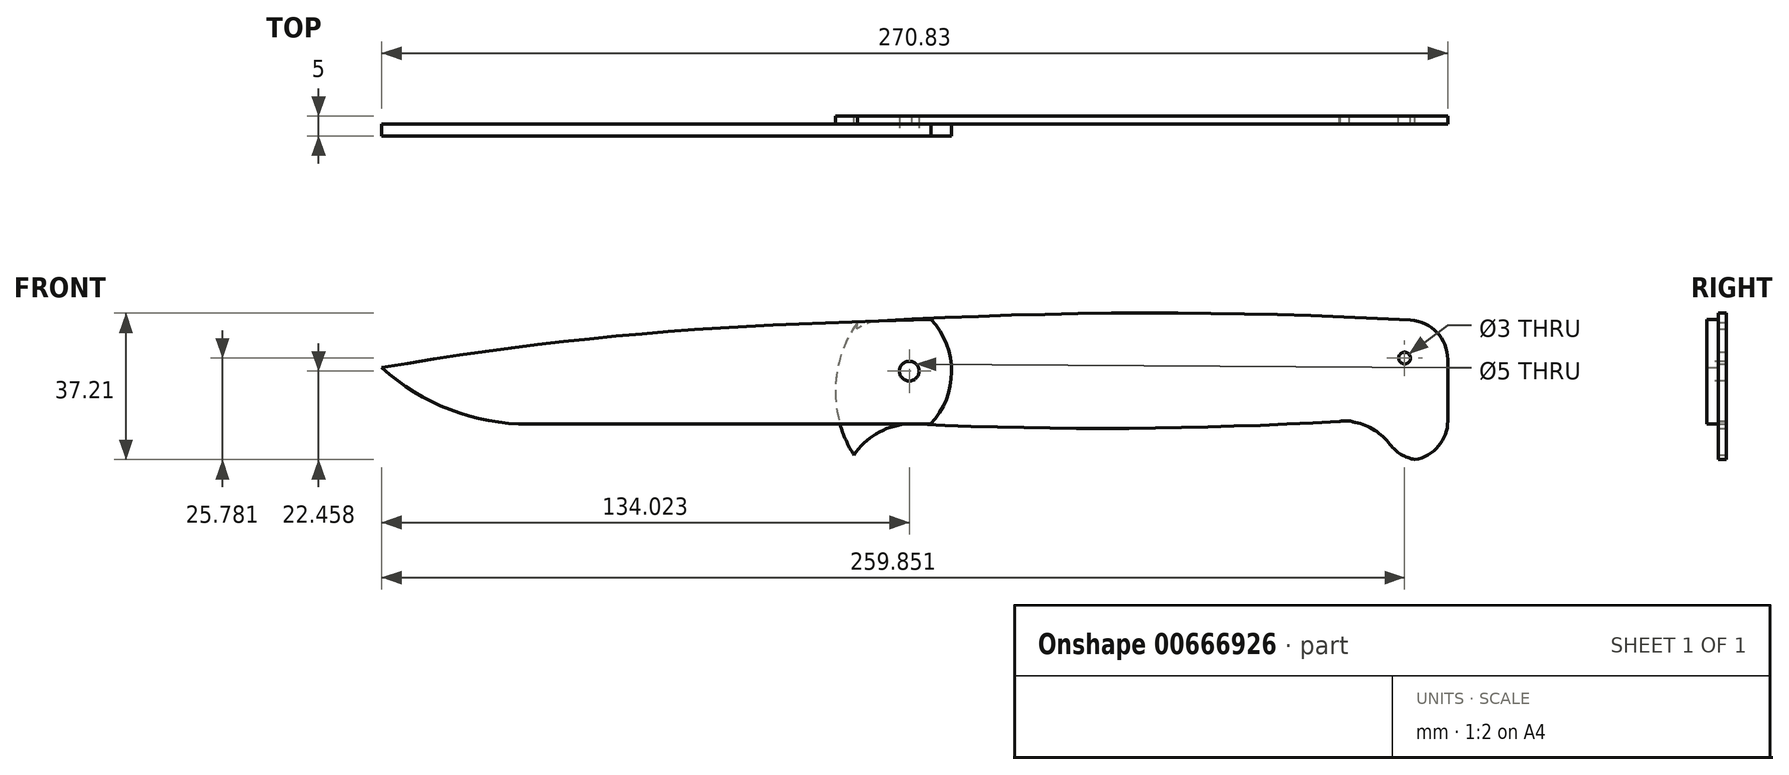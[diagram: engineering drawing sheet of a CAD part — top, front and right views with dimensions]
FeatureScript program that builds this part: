
annotation { "Feature Type Name" : "Feature", "Feature Type Description" : "" }
export const myFeature = defineFeature(function(context is Context, id is Id, definition is map)
    precondition{}
    {
        {
            var Q0;
            Q0=qCreatedBy(makeId("Front.planeOp"),FACE);
            var sketch = newSketch(context, id + "F0", { "sketchPlane" : qUnion([Q0])});
            skLineSegment(sketch, "E0", {"start": v(-53.95, 31.62) * mm, "end": v(96.05, 31.62) * mm});
            skLineSegment(sketch, "E1", {"start": v(96.05, 31.62) * mm, "end": v(96.05, -3.38) * mm});
            skLineSegment(sketch, "E2", {"start": v(96.05, -3.38) * mm, "end": v(71.05, -3.38) * mm});
            skLineSegment(sketch, "E3", {"start": v(71.05, -3.38) * mm, "end": v(71.05, 6.62) * mm});
            skLineSegment(sketch, "E4", {"start": v(71.05, 6.62) * mm, "end": v(-54.8, 6.62) * mm});
            skLineSegment(sketch, "E5", {"start": v(-54.8, 6.62) * mm, "end": v(-53.95, 31.62) * mm});
            skArc(sketch, "E6", {"start": v(96.05, 31.62) * mm, "mid": v(21.05, 33.97) * mm, "end": v(-53.95, 31.62) * mm});
            skArc(sketch, "E7", {"start": v(-54.8, 6.62) * mm, "mid": v(8.13, 4.68) * mm, "end": v(71.05, 6.62) * mm});
            skArc(sketch, "E8", {"start": v(-53.95, 31.62) * mm, "mid": v(-59.5, 14.87) * mm, "end": v(-54.8, -2.14) * mm});
            skArc(sketch, "E9", {"start": v(-40.07, 5.82) * mm, "mid": v(-48.44, 3.7) * mm, "end": v(-54.8, -2.14) * mm});
            skArc(sketch, "E10", {"start": v(83.55, -3.38) * mm, "mid": v(77.67, 4.08) * mm, "end": v(68.48, 6.46) * mm});
            skPoint(sketch, "E11.centerSnap0", {"position": v(-54.37, 19.12) * mm});
            skCircle(sketch, "E12", {"center": v(85.07, 22.54) * mm, "radius": 1.5 * mm});
            skSolve(sketch);
        }
        {
            var Q0;
            Q0=makeQuery(id+"F0.imprint","IMPRINT",FACE,{"disambiguationData":[TD([[makeQuery(id+"F0.imprint","IMPRINT",EDGE,{"derivedFrom":sQuery(id+"F0.wireOp",EDGE,"E0")}),-1.0]])]});
            var Q1;
            {var subQ0=sQuery(id+"F0.wireOp",EDGE,"E5");Q1=makeQuery(id+"F0.imprint","IMPRINT",FACE,{"disambiguationData":[TD([[makeQuery(id+"F0.imprint","IMPRINT",EDGE,{"derivedFrom":subQ0}),1.0]])]});}
            var Q2;
            Q2=makeQuery(id+"F0.imprint","IMPRINT",FACE,{"disambiguationData":[TD([[makeQuery(id+"F0.imprint","IMPRINT",EDGE,{"derivedFrom":sQuery(id+"F0.wireOp",EDGE,"E0")}),1.0]])]});
            var Q3;
            {var subQ0=sQuery(id+"F0.wireOp",EDGE,"E4");Q3=makeQuery(id+"F0.imprint","IMPRINT",FACE,{"disambiguationData":[TD([[makeQuery(id+"F0.imprint","IMPRINT",EDGE,{"derivedFrom":subQ0}),1.0]])]});}
            extrude(context, id + "F1", {"entities" : qUnion([Q0, Q1, Q2, Q3]), "depth" : 2 * mm, "offsetDistance" : 25 * mm});
        }
        {
            var Q0;
            Q0=makeQuery(id+"F1.opExtrude","SWEPT_EDGE",EDGE,{"disambiguationData":[OSD([sQuery(id+"F0.wireOp",EDGE,"E0"),sQuery(id+"F0.wireOp",EDGE,"E1"),sQuery(id+"F0.wireOp",EDGE,"E6")])]});
            var Q1;
            Q1=makeQuery(id+"F1.opExtrude","SWEPT_EDGE",EDGE,{"disambiguationData":[OSD([sQuery(id+"F0.wireOp",EDGE,"E1"),sQuery(id+"F0.wireOp",EDGE,"E2")])]});
            var Q2;
            Q2=makeQuery(id+"F1.opExtrude","SWEPT_EDGE",EDGE,{"disambiguationData":[OSD([sQuery(id+"F0.wireOp",EDGE,"E2"),sQuery(id+"F0.wireOp",EDGE,"E3")])]});
            var Q3;
            Q3=makeQuery(id+"F1.opExtrude","SWEPT_EDGE",EDGE,{"disambiguationData":[OSD([sQuery(id+"F0.wireOp",EDGE,"E0"),sQuery(id+"F0.wireOp",EDGE,"E5"),sQuery(id+"F0.wireOp",EDGE,"E6"),sQuery(id+"F0.wireOp",EDGE,"E8")])]});
            fillet(context, id + "F2", {"entities" : qUnion([Q0, Q1, Q2, Q3]), "radius" : 10 * mm, "tangentPropagation" : true, "allowEdgeOverflow" : false});
        }
        {
            var Q0;
            Q0=makeQuery(id+"F1.opExtrude","SWEPT_EDGE",EDGE,{"disambiguationData":[OSD([sQuery(id+"F0.wireOp",EDGE,"E8"),sQuery(id+"F0.wireOp",EDGE,"E9")])]});
            fillet(context, id + "F3", {"entities" : qUnion([Q0]), "radius" : 3 * mm, "tangentPropagation" : true, "allowEdgeOverflow" : false});
        }
        {
            var Q0;
            Q0=makeQuery(id+"F1.opExtrude","CAP_FACE",FACE,{"disambiguationData":[OSD([sQuery(id+"F0.wireOp",EDGE,"E1"),sQuery(id+"F0.wireOp",EDGE,"E2"),sQuery(id+"F0.wireOp",EDGE,"E3"),sQuery(id+"F0.wireOp",EDGE,"E6"),sQuery(id+"F0.wireOp",EDGE,"E7"),sQuery(id+"F0.wireOp",EDGE,"E8"),sQuery(id+"F0.wireOp",EDGE,"E9"),sQuery(id+"F0.wireOp",EDGE,"E10"),sQuery(id+"F0.wireOp",EDGE,"E11"),sQuery(id+"F0.wireOp",EDGE,"E12")])],"isStart":false});
            var sketch = newSketch(context, id + "F4", { "sketchPlane" : qUnion([Q0])});
            skLineSegment(sketch, "E13", {"start": v(-48.51, 31.95) * mm, "end": v(-68.74, 31.2) * mm});
            skPoint(sketch, "E14.orphan", {"position": v(-170.02, 0) * mm});
            skArc(sketch, "E15", {"start": v(-35.34, 5.74) * mm, "mid": v(-30, 19.03) * mm, "end": v(-35.22, 32.37) * mm});
            skLineSegment(sketch, "E16", {"start": v(-48.51, 31.95) * mm, "end": v(-35.22, 32.37) * mm});
            skArc(sketch, "E17", {"start": v(-68.74, 31.2) * mm, "mid": v(-121.95, 27.44) * mm, "end": v(-174.78, 20.1) * mm});
            skLineSegment(sketch, "E18", {"start": v(-35.34, 5.74) * mm, "end": v(-137.45, 5.74) * mm});
            skArc(sketch, "E19", {"start": v(-174.78, 20.1) * mm, "mid": v(-157.45, 9.45) * mm, "end": v(-137.45, 5.74) * mm});
            skCircle(sketch, "E20", {"center": v(-40.76, 19.22) * mm, "radius": 2.5 * mm});
            skSolve(sketch);
        }
        {
            var Q0;
            {var subQ13=sQuery(id+"F4.wireOp",EDGE,"E13");Q0=makeQuery(id+"F4.imprint","IMPRINT",FACE,{"disambiguationData":[TD([[makeQuery(id+"F4.imprint","IMPRINT",EDGE,{"derivedFrom":subQ13}),1.0]])]});}
            var Q1;
            {var subQ1=sQuery(id+"F4.wireOp",EDGE,"E15");Q1=makeQuery(id+"F4.imprint","IMPRINT",FACE,{"disambiguationData":[TD([[makeQuery(id+"F4.imprint","IMPRINT",EDGE,{"derivedFrom":subQ1}),1.0]])]});}
            var Q2;
            {var subQ0=sQuery(id+"F4.wireOp",EDGE,"jcSTLunK-culz-Bxrw-11Un-XH2iJDWFGlNg");var subQ1=sQuery(id+"F0.wireOp",EDGE,"E8");var subQ5=makeQuery(id+"F1.opExtrude","CAP_EDGE",EDGE,{"disambiguationData":[OSD([subQ1])],"isStart":false});var subQ6=makeQuery(id+"F4.imprint","INTERSECT",VERTEX,{"derivedFrom":[subQ5,subQ0]});Q2=makeQuery(id+"F4.imprint","IMPRINT",FACE,{"disambiguationData":[TD([[makeQuery(id+"F4.imprint","IMPRINT",EDGE,{"disambiguationData":[TD([[subQ6,1.0]])],"derivedFrom":subQ0}),1.0]])]});}
            extrude(context, id + "F5", {"entities" : qUnion([Q0, Q1, Q2]), "depth" : 3 * mm, "offsetDistance" : 25 * mm});
        }
        {
            var Q0;
            Q0=makeQuery(id+"F4.imprint","IMPRINT",FACE,{"disambiguationData":[TD([[makeQuery(id+"F4.imprint","IMPRINT",EDGE,{"derivedFrom":sQuery(id+"F4.wireOp",EDGE,"E20")}),1.0]])]});
            extrude(context, id + "F6", {"entities" : qUnion([Q0]), "operationType" : NewBodyOperationType.REMOVE, "endBound" : BoundingType.THROUGH_ALL, "oppositeDirection" : true, "depth" : 3 * mm, "offsetDistance" : 25 * mm});
        }
        {
            var Q0;
            Q0 = qSketchRegion(id + "F4", true);
            extrude(context, id + "F7", {"entities" : qUnion([Q0]), "operationType" : NewBodyOperationType.ADD, "depth" : 3 * mm, "offsetDistance" : 25 * mm});
        }
        {
            var Q0;
            {var subQ0=sQuery(id+"F0.wireOp",EDGE,"E5");Q0=makeQuery(id+"F0.imprint","IMPRINT",FACE,{"disambiguationData":[TD([[makeQuery(id+"F0.imprint","IMPRINT",EDGE,{"derivedFrom":subQ0}),1.0]])]});}
            extrude(context, id + "F8", {"entities" : qUnion([Q0]), "operationType" : NewBodyOperationType.ADD, "depth" : 3 * mm, "offsetDistance" : 25 * mm});
        }
        {
            var Q0;
            Q0=makeQuery(id+"F8.opExtrude","CAP_FACE",FACE,{"disambiguationData":[OSD([sQuery(id+"F0.wireOp",EDGE,"E5"),sQuery(id+"F0.wireOp",EDGE,"E7"),sQuery(id+"F0.wireOp",EDGE,"E8"),sQuery(id+"F0.wireOp",EDGE,"E9")])],"isStart":false});
            extrude(context, id + "F9", {"entities" : qUnion([Q0]), "operationType" : NewBodyOperationType.REMOVE, "oppositeDirection" : true, "depth" : 1 * mm, "offsetDistance" : 25 * mm});
        }
    });
